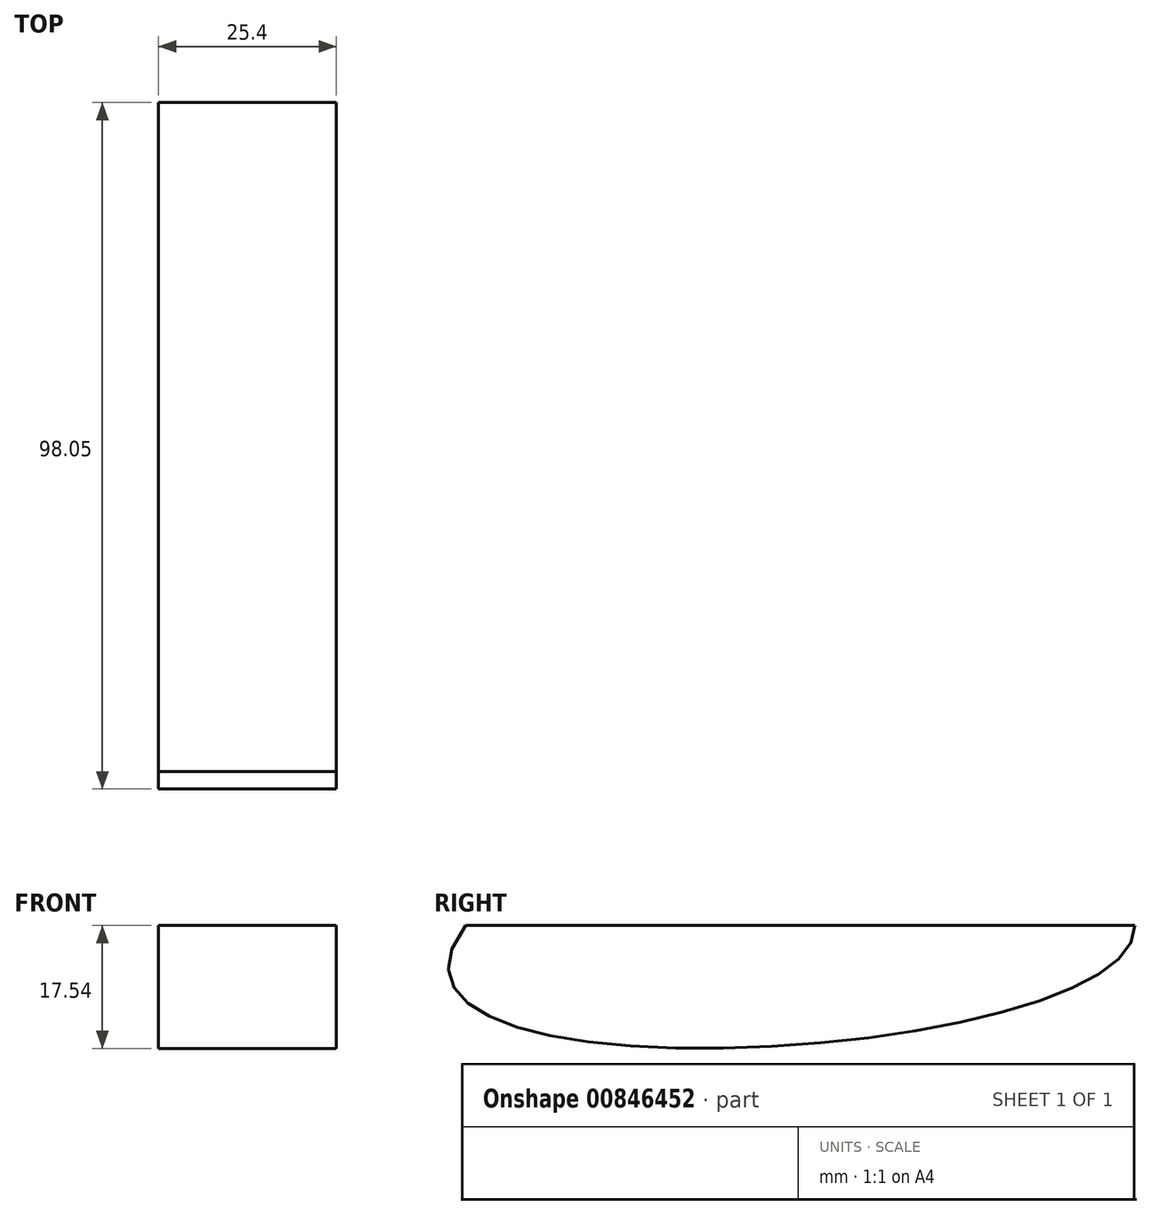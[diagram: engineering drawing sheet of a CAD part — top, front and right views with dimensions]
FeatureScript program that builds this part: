
annotation { "Feature Type Name" : "Feature", "Feature Type Description" : "" }
export const myFeature = defineFeature(function(context is Context, id is Id, definition is map)
    precondition{}
    {
        {
            var Q0;
            Q0=qCreatedBy(makeId("Right.planeOp"),FACE);
            var sketch = newSketch(context, id + "F0", { "sketchPlane" : qUnion([Q0])});
            skLineSegment(sketch, "E0", {"start": v(-48.65, 27.02) * mm, "end": v(46.9, 27.02) * mm});
            skFitSpline(sketch, "E1", {"points": [v(46.9, 27.02) * mm, v(-48.65, 27.02) * mm], "startDerivative": vector(1.67, -58.31) * mm, "endDerivative": vector(62.56, 81.06) * mm});
            skSolve(sketch);
        }
        {
            var Q0;
            Q0=makeQuery(id+"F0.imprint","IMPRINT",FACE,{"disambiguationData":[TD([[makeQuery(id+"F0.imprint","IMPRINT",EDGE,{"derivedFrom":sQuery(id+"F0.wireOp",EDGE,"E0")}),-1.0]])]});
            extrude(context, id + "F1", {"entities" : qUnion([Q0]), "depth" : 25.4 * mm, "offsetDistance" : 25.4 * mm});
        }
    });
